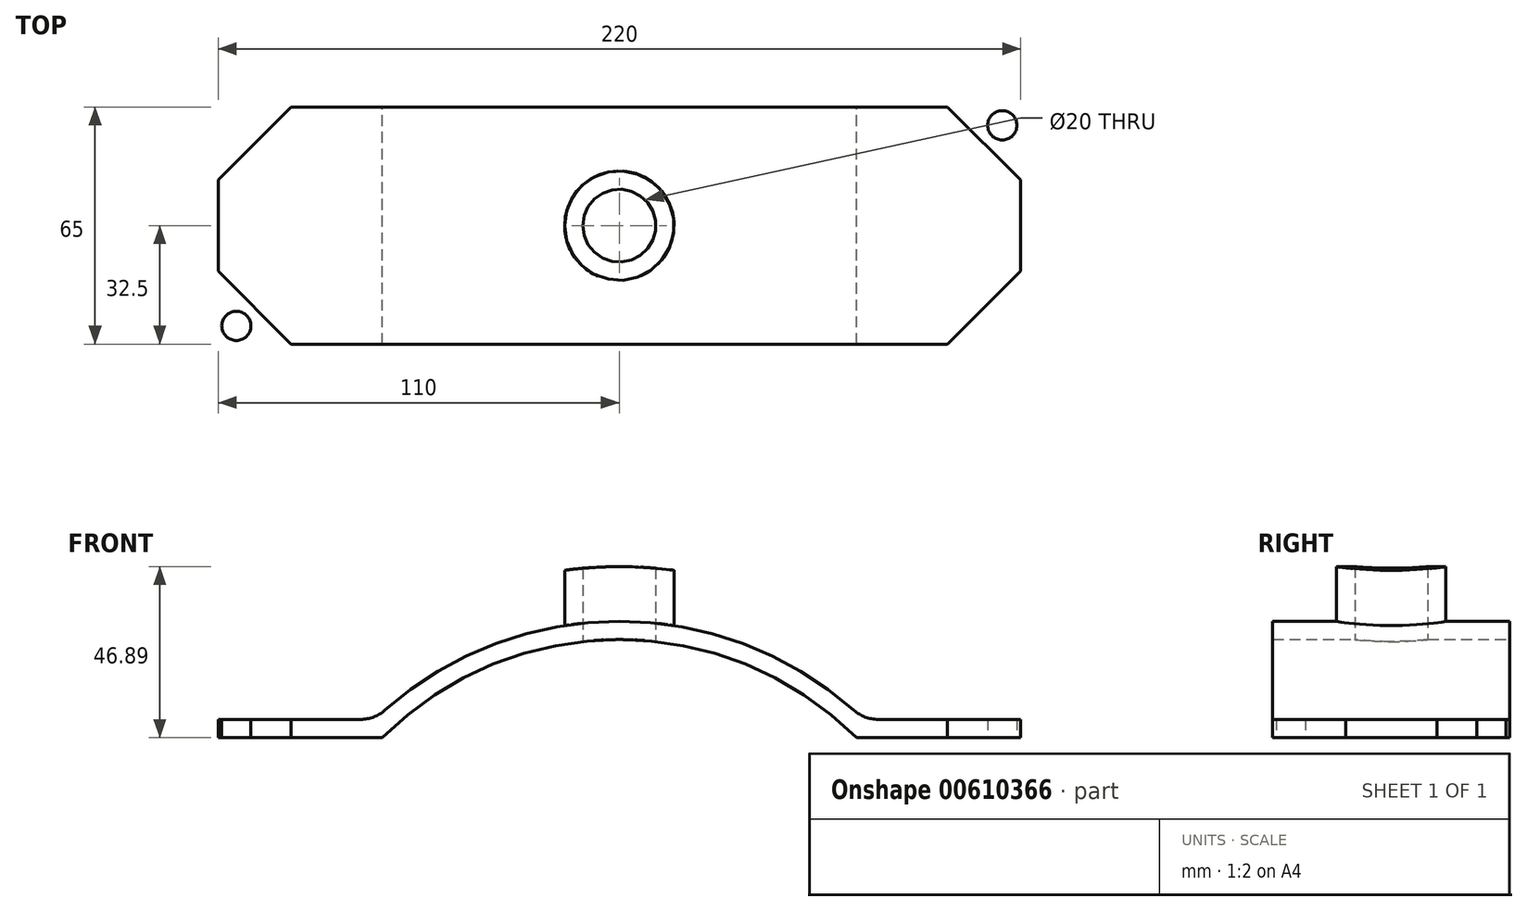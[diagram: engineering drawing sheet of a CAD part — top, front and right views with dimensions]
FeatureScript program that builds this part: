
annotation { "Feature Type Name" : "Feature", "Feature Type Description" : "" }
export const myFeature = defineFeature(function(context is Context, id is Id, definition is map)
    precondition{}
    {
        {
            var Q0;
            Q0=qCreatedBy(makeId("Front.planeOp"),FACE);
            var sketch = newSketch(context, id + "F0", { "sketchPlane" : qUnion([Q0])});
            skLineSegment(sketch, "E0", {"start": v(-115, 0) * mm, "end": v(-65, 0) * mm});
            skPoint(sketch, "E1", {"position": v(65, 0) * mm});
            skPoint(sketch, "E2", {"position": v(-65, 0) * mm});
            skLineSegment(sketch, "E3.trimOffspring", {"start": v(65, 0) * mm, "end": v(115, 0) * mm});
            skArc(sketch, "E4", {"start": v(65, 0) * mm, "mid": v(0, 26.9) * mm, "end": v(-65, 0) * mm});
            skLineSegment(sketch, "E5.0", {"start": v(-115, 5) * mm, "end": v(-67.04, 5) * mm});
            skArc(sketch, "E5.1", {"start": v(67.04, 5) * mm, "mid": v(0, 31.9) * mm, "end": v(-67.04, 5) * mm});
            skLineSegment(sketch, "E5.2", {"start": v(67.04, 5) * mm, "end": v(115, 5) * mm});
            skLineSegment(sketch, "E6.0", {"start": v(-115, 20) * mm, "end": v(-72.8, 20) * mm});
            skArc(sketch, "E6.1", {"start": v(72.8, 20) * mm, "mid": v(0, 46.9) * mm, "end": v(-72.8, 20) * mm});
            skLineSegment(sketch, "E6.2", {"start": v(72.8, 20) * mm, "end": v(115, 20) * mm});
            skLineSegment(sketch, "E7", {"start": v(-115, 20) * mm, "end": v(-115, 0) * mm});
            skLineSegment(sketch, "E8", {"start": v(115, 20) * mm, "end": v(115, 0) * mm});
            skLineSegment(sketch, "E9.bottom", {"start": v(-65, 0) * mm, "end": v(65, 0) * mm});
            skLineSegment(sketch, "E9.top", {"start": v(-65, -57.86) * mm, "end": v(65, -57.86) * mm});
            skLineSegment(sketch, "E9.left", {"start": v(-65, 0) * mm, "end": v(-65, -57.86) * mm});
            skLineSegment(sketch, "E9.right", {"start": v(65, 0) * mm, "end": v(65, -57.86) * mm});
            skLineSegment(sketch, "E10", {"start": v(-115, 20) * mm, "end": v(-115, 104.93) * mm});
            skLineSegment(sketch, "E11", {"start": v(-115, 104.93) * mm, "end": v(115, 104.93) * mm});
            skLineSegment(sketch, "E12", {"start": v(115, 104.93) * mm, "end": v(115, 20) * mm});
            skSolve(sketch);
        }
        {
            var Q0;
            {var subQ4=sQuery(id+"F0.wireOp",EDGE,"E0");Q0=makeQuery(id+"F0.imprint","IMPRINT",FACE,{"disambiguationData":[TD([[makeQuery(id+"F0.imprint","IMPRINT",EDGE,{"derivedFrom":subQ4}),1.0]])]});}
            extrude(context, id + "F1", {"entities" : qUnion([Q0]), "depth" : (75 / 2) * mm, "offsetDistance" : 25 * mm, "hasSecondDirection" : true, "secondDirectionOppositeDirection" : true, "secondDirectionDepth" : (75 / 2) * mm});
        }
        {
            var Q0;
            Q0=qCreatedBy(makeId("Top.planeOp"),FACE);
            var sketch = newSketch(context, id + "F2", { "sketchPlane" : qUnion([Q0])});
            skLineSegment(sketch, "E13.0", {"start": v(-115, 37.5) * mm, "end": v(-67.04, 37.5) * mm});
            skLineSegment(sketch, "E14.0", {"start": v(-115, -37.5) * mm, "end": v(-115, 37.5) * mm});
            skLineSegment(sketch, "E15.0", {"start": v(-115, -37.5) * mm, "end": v(-67.04, -37.5) * mm});
            skLineSegment(sketch, "E16.0", {"start": v(67.04, -37.5) * mm, "end": v(-67.04, -37.5) * mm});
            skLineSegment(sketch, "E17.0", {"start": v(67.04, -37.5) * mm, "end": v(115, -37.5) * mm});
            skLineSegment(sketch, "E18.0", {"start": v(115, -37.5) * mm, "end": v(115, 37.5) * mm});
            skLineSegment(sketch, "E19.0", {"start": v(67.04, 37.5) * mm, "end": v(115, 37.5) * mm});
            skLineSegment(sketch, "E20.0", {"start": v(67.04, 37.5) * mm, "end": v(-67.04, 37.5) * mm});
            skLineSegment(sketch, "E21.0", {"start": v(67.04, 32.5) * mm, "end": v(90, 32.5) * mm});
            skLineSegment(sketch, "E21.1", {"start": v(110, -12.5) * mm, "end": v(110, 12.5) * mm});
            skLineSegment(sketch, "E21.2", {"start": v(67.04, 32.5) * mm, "end": v(-67.04, 32.5) * mm});
            skLineSegment(sketch, "E21.3", {"start": v(67.04, -32.5) * mm, "end": v(90, -32.5) * mm});
            skLineSegment(sketch, "E21.4", {"start": v(-90, 32.5) * mm, "end": v(-67.04, 32.5) * mm});
            skLineSegment(sketch, "E21.5", {"start": v(-110, -12.5) * mm, "end": v(-110, 12.5) * mm});
            skLineSegment(sketch, "E21.6", {"start": v(-90, -32.5) * mm, "end": v(-67.04, -32.5) * mm});
            skLineSegment(sketch, "E21.7", {"start": v(67.04, -32.5) * mm, "end": v(-67.04, -32.5) * mm});
            skLineSegment(sketch, "E22", {"start": v(-90, 32.5) * mm, "end": v(-110, 12.5) * mm});
            skLineSegment(sketch, "E23", {"start": v(-90, -32.5) * mm, "end": v(-110, -12.5) * mm});
            skLineSegment(sketch, "E24.MirrorCS", {"start": v(90, 32.5) * mm, "end": v(110, 12.5) * mm});
            skLineSegment(sketch, "E25.MirrorCS", {"start": v(90, -32.5) * mm, "end": v(110, -12.5) * mm});
            skCircle(sketch, "E26", {"center": v(0, 0) * mm, "radius": 10 * mm});
            skCircle(sketch, "E27", {"center": v(0, 0) * mm, "radius": 15 * mm});
            skCircle(sketch, "E28", {"center": v(-105, 27.5) * mm, "radius": 4 * mm});
            skCircle(sketch, "E29.MirrorC", {"center": v(105, 27.5) * mm, "radius": 4 * mm});
            skCircle(sketch, "E30.MirrorC", {"center": v(-105, -27.5) * mm, "radius": 4 * mm});
            skCircle(sketch, "E31.MirrorC", {"center": v(105, -27.5) * mm, "radius": 4 * mm});
            skSolve(sketch);
        }
        {
            var Q0;
            Q0=makeQuery(id+"F2.imprint","IMPRINT",FACE,{"disambiguationData":[TD([[makeQuery(id+"F2.imprint","IMPRINT",EDGE,{"derivedFrom":sQuery(id+"F2.wireOp",EDGE,"E26")}),-1.0]])]});
            extrude(context, id + "F3", {"entities" : qUnion([Q0]), "operationType" : NewBodyOperationType.ADD, "depth" : 71.5 * mm, "offsetDistance" : 25 * mm});
        }
        {
            var Q0;
            Q0=makeQuery(id+"F2.imprint","IMPRINT",FACE,{"disambiguationData":[TD([[makeQuery(id+"F2.imprint","IMPRINT",EDGE,{"derivedFrom":sQuery(id+"F2.wireOp",EDGE,"E13.0")}),-1.0]])]});
            extrude(context, id + "F4", {"entities" : qUnion([Q0]), "operationType" : NewBodyOperationType.ADD, "depth" : 60 * mm, "offsetDistance" : 25 * mm});
        }
        {
            var Q0;
            Q0=makeQuery(id+"F0.imprint","IMPRINT",FACE,{"disambiguationData":[TD([[makeQuery(id+"F0.imprint","IMPRINT",EDGE,{"derivedFrom":sQuery(id+"F0.wireOp",EDGE,"E6.0")}),1.0]])]});
            var Q1;
            Q1=makeQuery(id+"F0.imprint","IMPRINT",FACE,{"disambiguationData":[TD([[makeQuery(id+"F0.imprint","IMPRINT",EDGE,{"derivedFrom":sQuery(id+"F0.wireOp",EDGE,"E9.bottom")}),-1.0]])]});
            var Q2;
            Q2=makeQuery(id+"F0.imprint","IMPRINT",FACE,{"disambiguationData":[TD([[makeQuery(id+"F0.imprint","IMPRINT",EDGE,{"derivedFrom":sQuery(id+"F0.wireOp",EDGE,"E4")}),1.0]])]});
            extrude(context, id + "F5", {"entities" : qUnion([Q0, Q1, Q2]), "operationType" : NewBodyOperationType.REMOVE, "oppositeDirection" : true, "depth" : 71 * mm, "offsetDistance" : 25 * mm, "hasSecondDirection" : true, "secondDirectionOppositeDirection" : false, "secondDirectionDepth" : 85 * mm});
        }
        {
            var Q0;
            Q0=makeQuery(id+"F2.imprint","IMPRINT",FACE,{"disambiguationData":[TD([[makeQuery(id+"F2.imprint","IMPRINT",EDGE,{"derivedFrom":sQuery(id+"F2.wireOp",EDGE,"E26")}),1.0]])]});
            var Q1;
            Q1=makeQuery(id+"F2.imprint","IMPRINT",FACE,{"disambiguationData":[TD([[makeQuery(id+"F2.imprint","IMPRINT",EDGE,{"derivedFrom":sQuery(id+"F2.wireOp",EDGE,"E30.MirrorC")}),-1.0]])]});
            var Q2;
            Q2=makeQuery(id+"F2.imprint","IMPRINT",FACE,{"disambiguationData":[TD([[makeQuery(id+"F2.imprint","IMPRINT",EDGE,{"derivedFrom":sQuery(id+"F2.wireOp",EDGE,"E28")}),1.0]])]});
            var Q3;
            Q3=makeQuery(id+"F2.imprint","IMPRINT",FACE,{"disambiguationData":[TD([[makeQuery(id+"F2.imprint","IMPRINT",EDGE,{"derivedFrom":sQuery(id+"F2.wireOp",EDGE,"E29.MirrorC")}),-1.0]])]});
            var Q4;
            Q4=makeQuery(id+"F2.imprint","IMPRINT",FACE,{"disambiguationData":[TD([[makeQuery(id+"F2.imprint","IMPRINT",EDGE,{"derivedFrom":sQuery(id+"F2.wireOp",EDGE,"E31.MirrorC")}),1.0]])]});
            extrude(context, id + "F6", {"entities" : qUnion([Q0, Q1, Q2, Q3, Q4]), "operationType" : NewBodyOperationType.REMOVE, "depth" : 88 * mm, "offsetDistance" : 25 * mm});
        }
        {
            var Q0;
            Q0=makeQuery(id+"F1.opExtrude","SWEPT_EDGE",EDGE,{"disambiguationData":[OSD([sQuery(id+"F0.wireOp",EDGE,"E5.1"),sQuery(id+"F0.wireOp",EDGE,"E5.2")])]});
            var Q1;
            Q1=makeQuery(id+"F1.opExtrude","SWEPT_EDGE",EDGE,{"disambiguationData":[OSD([sQuery(id+"F0.wireOp",EDGE,"E5.0"),sQuery(id+"F0.wireOp",EDGE,"E5.1")])]});
            var Q2;
            Q2=makeQuery(id+"F4.boolean.opBoolean","MERGE",EDGE,{"derivedFrom":[makeQuery(id+"F1.opExtrude","CAP_EDGE",EDGE,{"disambiguationData":[OSD([sQuery(id+"F0.wireOp",EDGE,"E8")])],"isStart":false}),makeQuery(id+"F4.opExtrude","SWEPT_EDGE",EDGE,{"disambiguationData":[OSD([sQuery(id+"F2.wireOp",EDGE,"E17.0"),sQuery(id+"F2.wireOp",EDGE,"E18.0")])]})]});
            var Q3;
            Q3=makeQuery(id+"F4.boolean.opBoolean","MERGE",EDGE,{"derivedFrom":[makeQuery(id+"F1.opExtrude","CAP_EDGE",EDGE,{"disambiguationData":[OSD([sQuery(id+"F0.wireOp",EDGE,"E8")])],"isStart":true}),makeQuery(id+"F4.opExtrude","SWEPT_EDGE",EDGE,{"disambiguationData":[OSD([sQuery(id+"F2.wireOp",EDGE,"E18.0"),sQuery(id+"F2.wireOp",EDGE,"E19.0")])]})]});
            var Q4;
            Q4=makeQuery(id+"F4.boolean.opBoolean","MERGE",EDGE,{"derivedFrom":[makeQuery(id+"F1.opExtrude","CAP_EDGE",EDGE,{"disambiguationData":[OSD([sQuery(id+"F0.wireOp",EDGE,"E7")])],"isStart":false}),makeQuery(id+"F4.opExtrude","SWEPT_EDGE",EDGE,{"disambiguationData":[OSD([sQuery(id+"F2.wireOp",EDGE,"E14.0"),sQuery(id+"F2.wireOp",EDGE,"E15.0")])]})]});
            var Q5;
            Q5=makeQuery(id+"F4.boolean.opBoolean","MERGE",EDGE,{"derivedFrom":[makeQuery(id+"F1.opExtrude","CAP_EDGE",EDGE,{"disambiguationData":[OSD([sQuery(id+"F0.wireOp",EDGE,"E7")])],"isStart":true}),makeQuery(id+"F4.opExtrude","SWEPT_EDGE",EDGE,{"disambiguationData":[OSD([sQuery(id+"F2.wireOp",EDGE,"E13.0"),sQuery(id+"F2.wireOp",EDGE,"E14.0")])]})]});
            fillet(context, id + "F7", {"entities" : qUnion([Q0, Q1, Q2, Q3, Q4, Q5]), "radius" : 10 * mm, "tangentPropagation" : true, "allowEdgeOverflow" : false});
        }
    });
